# Revit family: IS_LDV_T5518_BIM_NL
name_source: partatom
category: Plumbing Fixtures
units: mm (PartAtom-declared; Revit-internal decimal feet)

## family parameters
Cut with Voids When Loaded = No
Host = Face
Maintain Annotation Orientation = No
OmniClass Number = 23.45.05.14.21.11
OmniClass Title = Bath/Shower Units
Part Type = Normal
Room Calculation Point = No
Round Connector Dimension = Use Diameter
Shared = Yes

## types (1)
- T5518EN - LDV F/S BATH 180X85 WHITE
    Accesoires = https://www.idealstandard.nl
    Accessories = https://www.idealstandard.nl
    Afmetingen = 1764 x 848 x 563 mm
    AfstandsEenheid = millimeter
    Afwerking = wit mat
    AreaUnits = millimeter
    Artikelnummer = T5518EN
    Artikelomschrijving = LDV | Vrijstaand bad 1760x840x565 mm, zonder kraangat, met overloop, zonder waste
    Assembly Code = C1030200
    AssetType = Vast
    Auteur = Ideal Standard
    BIMObjectName = ISI_IdealStandard_Baths_T5518
    BREEAM = No
    BarCode = 8014140514589
    Barcode = 8014140514589
    BathType = Huiselijk
    Beschrijvinggarantie = Fabrieksgarantie
    BimObjectNaam = ISI_IdealStandard_Baths_T5518
    Brand = Ideal Standard
    Breedte = 1763,69032276712
    Category = SanitaryTerminal_BATH_UK
    Color = wit mat
    ConnectionType = Loodgieter
    CurrencyUnit = €
    Default Elevation = 0 mm  [stored 0 ft]
    Description = LDV | Vrijstaand bad 1760x840x565 mm, zonder kraangat, met overloop, zonder waste
    Diepte = 847,713097801531
    DrainSize = 52 mm
    DurationUnit = jaar
    DuurEenheid = jaar
    ECA = No
    EPD = https://www.idealstandard.nl
    Eigenschappen = LDV | Vrijstaand bad 1760x840x565 mm in mat wit afwerking, zonder kraangat, met overloop, zonder waste | Antibacterieel
    ExpectedLife = 30
    Features = LDV | Vrijstaand bad 1760x840x565 mm in mat wit afwerking, zonder kraangat, met overloop, zonder waste | Antibacterieel
    Finish = wit mat
    Garantieunits = jaar
    GemaaktOp = 2024-04-25
    HasGrabHandles = No
    Help = https://www.idealstandard.nl
    Hoogte = 563,3217041093
    Hulp = https://www.idealstandard.nl
    IfcExportAs = IfcSanitaryTerminalType
    IfcExportType = BATH
    Installatieinstructies = https://www.idealstandard.nl
    InstallationInstructions = https://www.idealstandard.nl
    Kleur = wit mat
    Lengte = 847,713097801531
    LinearUnits = millimeter
    Manufacturer = Ideal Standard
    ManufacturerURL = https://www.idealstandard.nl
    Materiaal = Mineraal gieten
    Material = Mineraal gieten
    MaterialThickness = 0 mm  [stored 0 ft]
    Merk = Ideal Standard
    Model = T5518EN
    ModelNumber = T5518EN
    ModelReference = LDV | Vrijstaand bad 1760x840x565 mm, zonder kraangat, met overloop, zonder waste
    NBSDescription = Baths
    NBSReference = 45-35-70/311
    Name = ISI_Baths_LDV_T5518_IdealStandard
    NettWeight = 180.00
    Nettogewicht = 180.00
    NominalDepth = 848 mm
    NominalHeight = 563 mm
    NominalLength = 848 mm
    NominalWidth = 1764 mm
    ProductInformation = https://www.idealstandard.nl
    ProductSoort = Bad
    Productinformatie = https://www.idealstandard.nl
    Shape = Gebeeldhouwd
    Size = 1764 x 848 x 563 mm
    Space = Intern
    SpareParts = https://www.idealstandard.nl
    TMV3 = No
    Telefoonnummer = 077 355 08 08
    Typeconnectie = Loodgieter
    URL = https://www.idealstandard.nl
    Uniclass2 = Pr_40_20_06_08
    Uniclass2015Code = Pr_40_20_06_08
    Uniclass2015Description = Baths
    Uniclass2015Reference = Pr_40_20_06_08  Baths
    Uniclass2015Title = Baths
    Uniclass2015Version = Products v1.33
    Urlproducent = https://www.idealstandard.nl
    ValutaEenheid = €
    Versie = 1
    Version = 1
    Vervangingskosten = 0
    VolumeUnits = Liter
    Volumeunits = Liter
    Vorm = Gebeeldhouwd
    WRAS = No
    WaarborgGarantieInstallatie = Fabrikanten Garantie
    WarrantyDescription = Fabrikanten Garantie
    WarrantyDurationParts = 25
    WarrantyDurationUnit = jaar
    WarrantyGuarantorParts = https://www.idealstandard.nl
    WaterEfficientProduct = No
    Wisselstukken = https://www.idealstandard.nl

note: [stored X ft] marks values corroborated as IEEE doubles in the binary element streams (Revit-internal decimal feet)

## geometry (parser evidence)
native form markers: Sweep x4
no freeform markers — native parametric forms only
